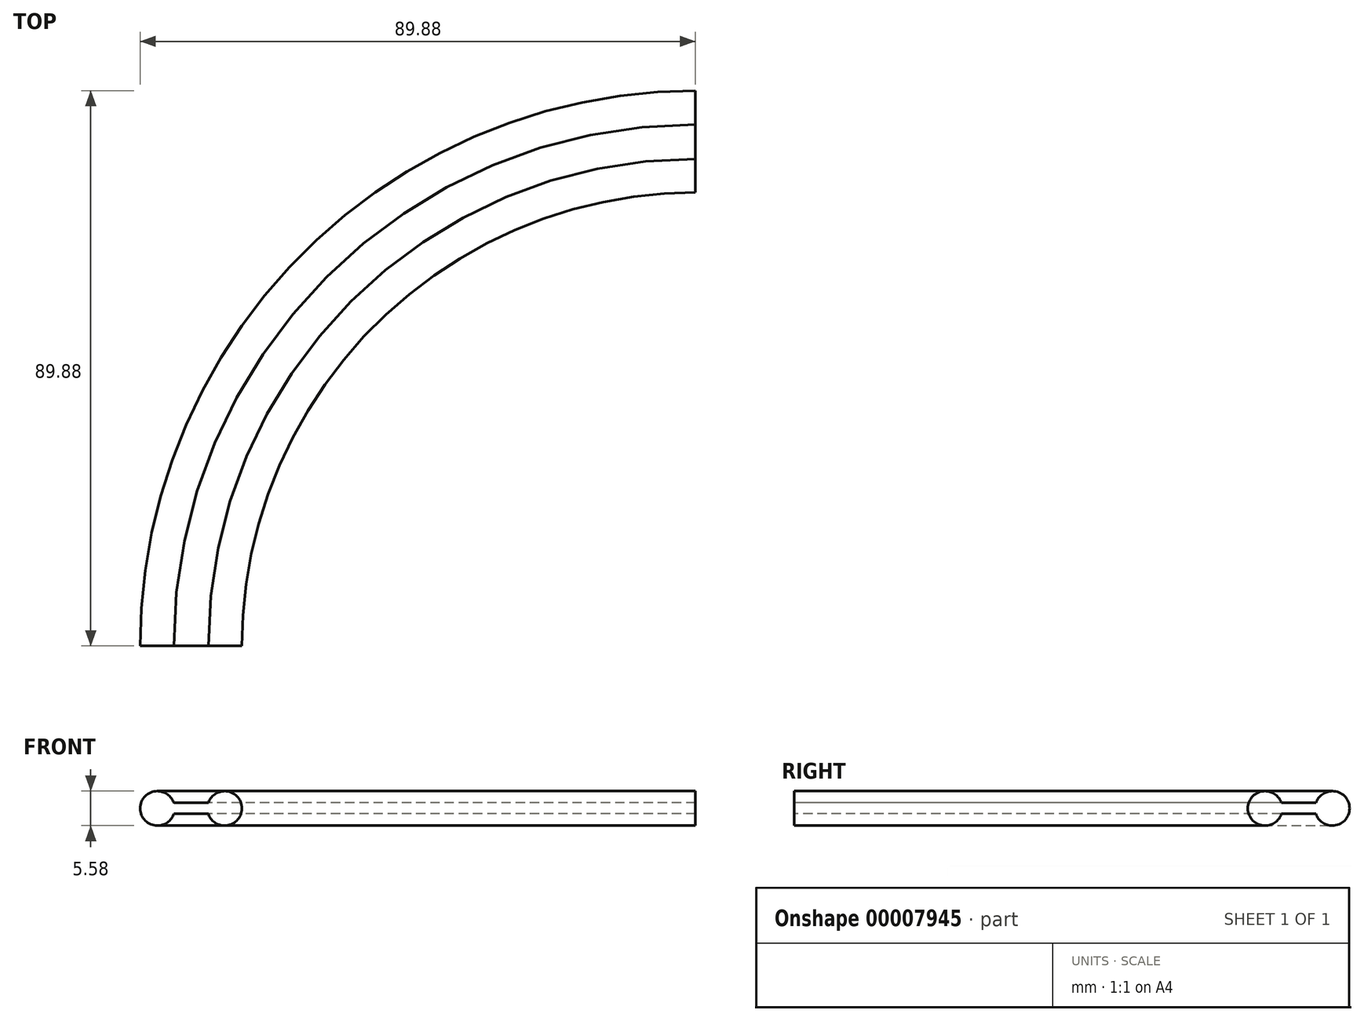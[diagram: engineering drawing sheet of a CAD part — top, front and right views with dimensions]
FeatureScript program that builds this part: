
annotation { "Feature Type Name" : "Feature", "Feature Type Description" : "" }
export const myFeature = defineFeature(function(context is Context, id is Id, definition is map)
    precondition{}
    {
        {
            var Q0;
            Q0=qCreatedBy(makeId("Front.planeOp"),FACE);
            var sketch = newSketch(context, id + "F0", { "sketchPlane" : qUnion([Q0])});
            skCircle(sketch, "E0", {"center": v(-76.2, 0) * mm, "radius": 2.8 * mm});
            skCircle(sketch, "E1", {"center": v(-87.09, 0) * mm, "radius": 2.8 * mm});
            skLineSegment(sketch, "E2", {"start": v(-84.44, 0.89) * mm, "end": v(-78.85, 0.89) * mm});
            skLineSegment(sketch, "E3", {"start": v(-84.44, -0.89) * mm, "end": v(-78.85, -0.89) * mm});
            skSolve(sketch);
        }
        {
            var Q0;
            Q0=qCreatedBy(makeId("Front.planeOp"),FACE);
            var sketch = newSketch(context, id + "F1", { "sketchPlane" : qUnion([Q0])});
            skLineSegment(sketch, "E4", {"start": v(0, 13.63) * mm, "end": v(0, -14.08) * mm, "construction": true});
            skSolve(sketch);
        }
        {
            var Q0;
            Q0 = qSketchRegion(id + "F0", true);
            var Q1;
            Q1=sQuery(id+"F1.wireOp",EDGE,"E4");
            revolve(context, id + "F2", {"entities" : qUnion([Q0]), "axis" : qUnion([Q1]), "revolveType" : RevolveType.ONE_DIRECTION, "angle" : 90 * degree});
        }
    });
